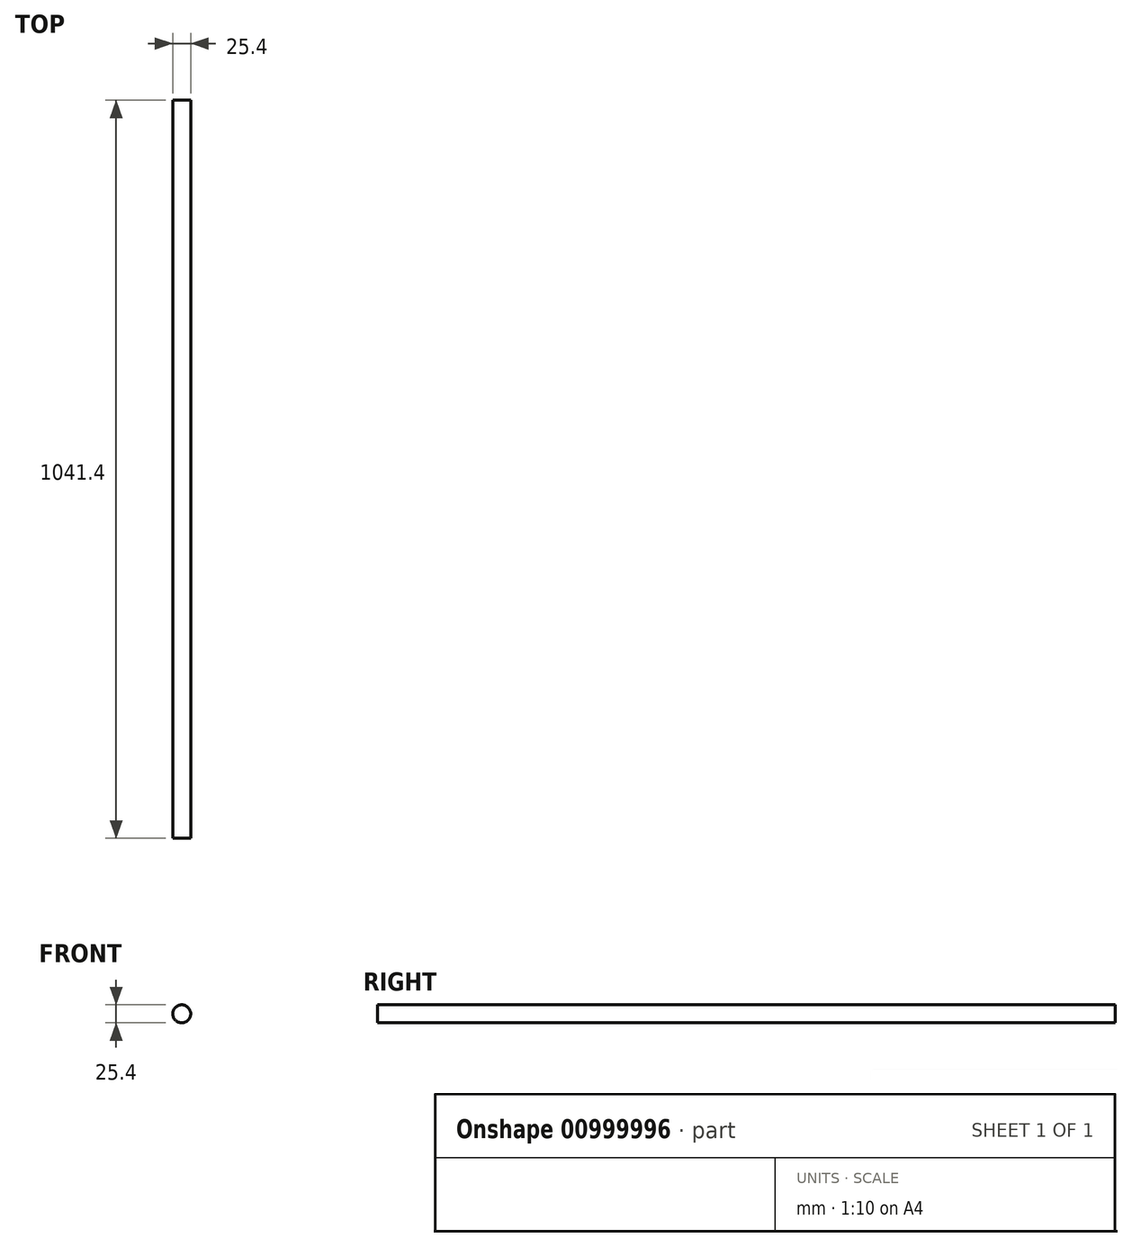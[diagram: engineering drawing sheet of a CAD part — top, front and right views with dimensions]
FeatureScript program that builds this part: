
annotation { "Feature Type Name" : "Feature", "Feature Type Description" : "" }
export const myFeature = defineFeature(function(context is Context, id is Id, definition is map)
    precondition{}
    {
        {
            var Q0;
            Q0=qCreatedBy(makeId("Front.planeOp"),FACE);
            var sketch = newSketch(context, id + "F0", { "sketchPlane" : qUnion([Q0])});
            skCircle(sketch, "E0", {"center": v(0, 0) * mm, "radius": 12.7 * mm});
            skSolve(sketch);
        }
        {
            var Q0;
            Q0=makeQuery(id+"F0.imprint","IMPRINT",FACE,{"disambiguationData":[TD([[makeQuery(id+"F0.imprint","IMPRINT",EDGE,{"derivedFrom":sQuery(id+"F0.wireOp",EDGE,"E0")}),1.0]])]});
            extrude(context, id + "F1", {"entities" : qUnion([Q0]), "depth" : 1041.4 * mm, "offsetDistance" : 25.4 * mm});
        }
    });
